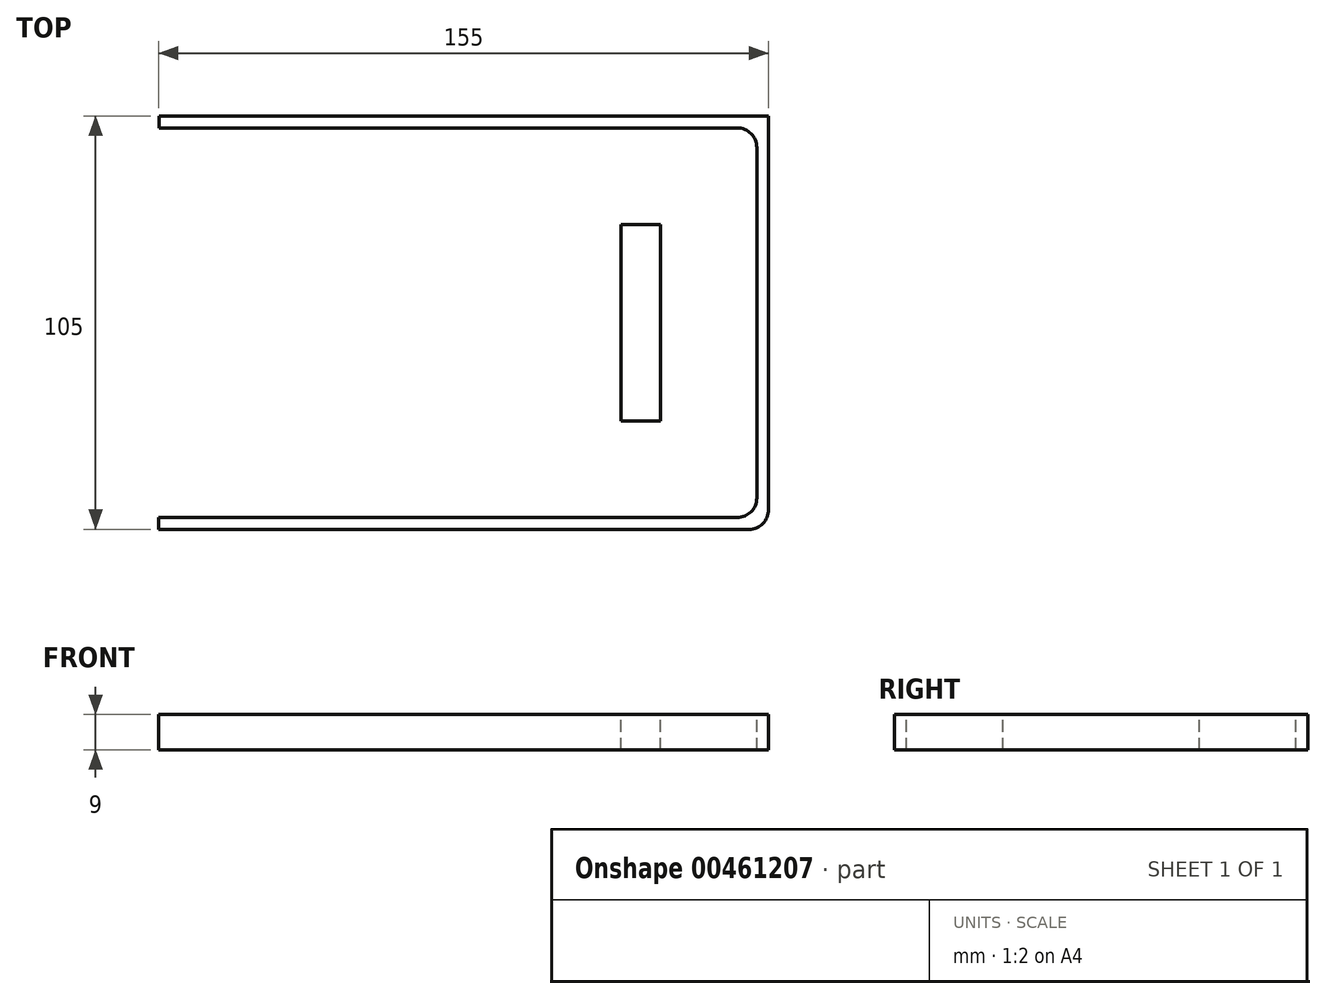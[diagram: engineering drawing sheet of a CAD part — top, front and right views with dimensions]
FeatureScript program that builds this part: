
annotation { "Feature Type Name" : "Feature", "Feature Type Description" : "" }
export const myFeature = defineFeature(function(context is Context, id is Id, definition is map)
    precondition{}
    {
        {
            var Q0;
            Q0=qCreatedBy(makeId("Top.planeOp"),FACE);
            var sketch = newSketch(context, id + "F0", { "sketchPlane" : qUnion([Q0])});
            skLineSegment(sketch, "E0.bottom", {"start": v(100, 75) * mm, "end": v(-100, 75) * mm});
            skLineSegment(sketch, "E0.top", {"start": v(100, -75) * mm, "end": v(-100, -75) * mm});
            skLineSegment(sketch, "E0.left", {"start": v(100, 75) * mm, "end": v(100, -75) * mm});
            skLineSegment(sketch, "E0.right", {"start": v(-100, 75) * mm, "end": v(-100, -75) * mm});
            skPoint(sketch, "E0.middle", {"position": v(0, 0) * mm});
            skSolve(sketch);
        }
        {
            var Q0;
            Q0=makeQuery(id+"F0.imprint","IMPRINT",FACE,{"disambiguationData":[TD([[makeQuery(id+"F0.imprint","IMPRINT",EDGE,{"derivedFrom":sQuery(id+"F0.wireOp",EDGE,"E0.bottom")}),1.0]])]});
            extrude(context, id + "F1", {"entities" : qUnion([Q0]), "depth" : 9 * mm, "offsetDistance" : 25 * mm});
        }
        {
            var Q0;
            Q0=makeQuery(id+"F1.opExtrude","CAP_FACE",FACE,{"disambiguationData":[OSD([sQuery(id+"F0.wireOp",EDGE,"E0.bottom"),sQuery(id+"F0.wireOp",EDGE,"E0.top"),sQuery(id+"F0.wireOp",EDGE,"E0.left"),sQuery(id+"F0.wireOp",EDGE,"E0.right")])],"isStart":false});
            var sketch = newSketch(context, id + "F2", { "sketchPlane" : qUnion([Q0])});
            skLineSegment(sketch, "E1.bottom", {"start": v(87.5, 60.44) * mm, "end": v(-87.5, 60.44) * mm});
            skLineSegment(sketch, "E1.top", {"start": v(87.5, -64.56) * mm, "end": v(-77.5, -64.56) * mm});
            skLineSegment(sketch, "E1.left", {"start": v(87.5, 60.44) * mm, "end": v(87.5, -64.56) * mm});
            skLineSegment(sketch, "E1.right", {"start": v(-87.5, 60.44) * mm, "end": v(-87.5, 34.72) * mm});
            skPoint(sketch, "E1.middle", {"position": v(0, -2.06) * mm});
            skLineSegment(sketch, "E2.bottom", {"start": v(-87.5, 29.72) * mm, "end": v(-46, 29.72) * mm});
            skLineSegment(sketch, "E3", {"start": v(-46, -38.28) * mm, "end": v(-87.5, -38.28) * mm});
            skLineSegment(sketch, "E4", {"start": v(-41, -38.28) * mm, "end": v(-46, -38.28) * mm});
            skLineSegment(sketch, "E5", {"start": v(-41, 34.72) * mm, "end": v(-87.5, 34.72) * mm});
            skLineSegment(sketch, "E6.trimOffspring", {"start": v(-87.5, -38.28) * mm, "end": v(-87.5, -64.56) * mm});
            skLineSegment(sketch, "E7", {"start": v(-6, -30.28) * mm, "end": v(-6, 26.72) * mm});
            skLineSegment(sketch, "E8", {"start": v(-74.36, 50.44) * mm, "end": v(60.64, 50.44) * mm});
            skLineSegment(sketch, "E9", {"start": v(60.64, 47.44) * mm, "end": v(-74.36, 47.44) * mm});
            skLineSegment(sketch, "E10", {"start": v(-74.36, 50.44) * mm, "end": v(-77.36, 50.44) * mm});
            skLineSegment(sketch, "E11", {"start": v(-77.36, 50.44) * mm, "end": v(-77.36, 47.44) * mm});
            skLineSegment(sketch, "E12", {"start": v(-77.36, 47.44) * mm, "end": v(-74.36, 47.44) * mm});
            skLineSegment(sketch, "E13", {"start": v(-87.5, -64.56) * mm, "end": v(-77.5, -64.56) * mm});
            skLineSegment(sketch, "E14", {"start": v(-77.5, -54.56) * mm, "end": v(60.64, -54.56) * mm});
            skLineSegment(sketch, "E15", {"start": v(60.64, -51.56) * mm, "end": v(-77.5, -51.56) * mm});
            skLineSegment(sketch, "E16", {"start": v(-77.5, -54.56) * mm, "end": v(-77.5, -51.56) * mm});
            skLineSegment(sketch, "E17", {"start": v(60.64, 47.44) * mm, "end": v(57.64, 47.44) * mm});
            skLineSegment(sketch, "E18", {"start": v(60.64, 50.44) * mm, "end": v(77.5, 50.44) * mm});
            skLineSegment(sketch, "E19", {"start": v(77.5, 50.44) * mm, "end": v(77.5, -54.56) * mm});
            skLineSegment(sketch, "E20", {"start": v(77.5, -54.56) * mm, "end": v(60.64, -54.56) * mm});
            skLineSegment(sketch, "E21", {"start": v(77.5, 50.44) * mm, "end": v(77.5, 47.44) * mm});
            skLineSegment(sketch, "E22", {"start": v(69.5, 47.44) * mm, "end": v(60.64, 47.44) * mm});
            skLineSegment(sketch, "E23", {"start": v(77.5, 50.44) * mm, "end": v(74.5, 50.44) * mm});
            skLineSegment(sketch, "E24", {"start": v(74.5, 42.44) * mm, "end": v(74.5, -46.56) * mm});
            skLineSegment(sketch, "E25", {"start": v(60.64, -51.56) * mm, "end": v(69.5, -51.56) * mm});
            skPoint(sketch, "E26.end.orphan", {"position": v(77.5, 48.67) * mm});
            skArc(sketch, "E27.filletArc", {"start": v(74.5, 42.44) * mm, "mid": v(73.03, 45.97) * mm, "end": v(69.5, 47.44) * mm});
            skPoint(sketch, "E28.visualSharp", {"position": v(74.5, -51.56) * mm});
            skArc(sketch, "E28.filletArc", {"start": v(69.5, -51.56) * mm, "mid": v(73.03, -50.1) * mm, "end": v(74.5, -46.56) * mm});
            skLineSegment(sketch, "E29", {"start": v(-87.5, 29.72) * mm, "end": v(-38.5, 29.72) * mm});
            skLineSegment(sketch, "E30", {"start": v(-38.5, 29.72) * mm, "end": v(-38.5, 26.72) * mm});
            skLineSegment(sketch, "E31", {"start": v(-38.5, 26.72) * mm, "end": v(-33.5, 26.72) * mm});
            skLineSegment(sketch, "E32", {"start": v(-33.5, 26.72) * mm, "end": v(-33.5, 34.72) * mm});
            skLineSegment(sketch, "E33", {"start": v(-33.5, 34.72) * mm, "end": v(-41, 34.72) * mm});
            skLineSegment(sketch, "E34", {"start": v(-100, -0.26) * mm, "end": v(-100, -3.86) * mm});
            skLineSegment(sketch, "E35", {"start": v(-100, -0.26) * mm, "end": v(-92.5, -0.26) * mm});
            skLineSegment(sketch, "E36", {"start": v(-100, -3.86) * mm, "end": v(-92.5, -3.86) * mm});
            skLineSegment(sketch, "E37", {"start": v(-87.5, -6.86) * mm, "end": v(-92.5, -3.86) * mm});
            skLineSegment(sketch, "E38", {"start": v(-92.5, -0.26) * mm, "end": v(-87.5, 2.74) * mm});
            skLineSegment(sketch, "E39", {"start": v(-87.5, 2.74) * mm, "end": v(-87.5, 29.72) * mm});
            skLineSegment(sketch, "E40", {"start": v(-87.5, -6.86) * mm, "end": v(-87.5, -33.28) * mm});
            skLineSegment(sketch, "E41", {"start": v(-87.5, -33.28) * mm, "end": v(-38.5, -33.28) * mm});
            skLineSegment(sketch, "E42", {"start": v(-38.5, -33.28) * mm, "end": v(-38.5, -30.28) * mm});
            skLineSegment(sketch, "E43", {"start": v(-38.5, -30.28) * mm, "end": v(-33.5, -30.28) * mm});
            skLineSegment(sketch, "E44", {"start": v(-33.5, -30.28) * mm, "end": v(-33.5, -38.28) * mm});
            skLineSegment(sketch, "E45", {"start": v(-33.5, -38.28) * mm, "end": v(-41, -38.28) * mm});
            skPoint(sketch, "E46.start.orphan", {"position": v(-41, -30.28) * mm});
            skLineSegment(sketch, "E47", {"start": v(0, -2.06) * mm, "end": v(40, -2.06) * mm});
            skLineSegment(sketch, "E48", {"start": v(40, -2.06) * mm, "end": v(40, 35.44) * mm});
            skLineSegment(sketch, "E49", {"start": v(40, -2.06) * mm, "end": v(40, -39.56) * mm});
            skPoint(sketch, "E50.end.orphan", {"position": v(42.97, -39.56) * mm});
            skLineSegment(sketch, "E51", {"start": v(40, 35.44) * mm, "end": v(50, 35.44) * mm});
            skLineSegment(sketch, "E52", {"start": v(50, 35.44) * mm, "end": v(50, -39.56) * mm});
            skLineSegment(sketch, "E53", {"start": v(50, -39.56) * mm, "end": v(40, -39.56) * mm});
            skLineSegment(sketch, "E54", {"start": v(40, -2.06) * mm, "end": v(40, 22.94) * mm});
            skLineSegment(sketch, "E55", {"start": v(40, 22.94) * mm, "end": v(50, 22.94) * mm});
            skLineSegment(sketch, "E56", {"start": v(40, -2.06) * mm, "end": v(40, -27.06) * mm});
            skLineSegment(sketch, "E57", {"start": v(40, -27.06) * mm, "end": v(50, -27.06) * mm});
            skSolve(sketch);
        }
        {
            var Q0;
            Q0=makeQuery(id+"F2.imprint","IMPRINT",FACE,{"disambiguationData":[TD([[makeQuery(id+"F2.imprint","IMPRINT",EDGE,{"derivedFrom":sQuery(id+"F2.wireOp",EDGE,"E1.bottom")}),1.0]])]});
            var Q1;
            Q1=makeQuery(id+"F2.imprint","IMPRINT",FACE,{"disambiguationData":[TD([[makeQuery(id+"F2.imprint","IMPRINT",EDGE,{"derivedFrom":sQuery(id+"F2.wireOp",EDGE,"E54")}),-1.0]])]});
            var Q2;
            Q2=makeQuery(id+"F2.imprint","IMPRINT",FACE,{"disambiguationData":[TD([[makeQuery(id+"F2.imprint","IMPRINT",EDGE,{"derivedFrom":sQuery(id+"F2.wireOp",EDGE,"E48")}),-1.0]])]});
            var Q3;
            Q3=makeQuery(id+"F2.imprint","IMPRINT",FACE,{"disambiguationData":[TD([[makeQuery(id+"F2.imprint","IMPRINT",EDGE,{"derivedFrom":sQuery(id+"F2.wireOp",EDGE,"E49")}),1.0]])]});
            var Q4;
            Q4=makeQuery(id+"F2.imprint","IMPRINT",FACE,{"disambiguationData":[TD([[makeQuery(id+"F2.imprint","IMPRINT",EDGE,{"derivedFrom":sQuery(id+"F2.wireOp",EDGE,"E1.bottom")}),-1.0]])]});
            extrude(context, id + "F3", {"entities" : qUnion([Q0, Q1, Q2, Q3, Q4]), "operationType" : NewBodyOperationType.REMOVE, "oppositeDirection" : true, "depth" : 25 * mm, "offsetDistance" : 25 * mm});
        }
        {
            var Q0;
            Q0=makeQuery(id+"F3.boolean.opBoolean","COPY",EDGE,{"derivedFrom":makeQuery(id+"F3.opExtrude","SWEPT_EDGE",EDGE,{"disambiguationData":[OSD([sQuery(id+"F2.wireOp",EDGE,"E21"),sQuery(id+"F2.wireOp",EDGE,"E23")])]})});
            var Q1;
            Q1=makeQuery(id+"F3.boolean.opBoolean","COPY",EDGE,{"derivedFrom":makeQuery(id+"F3.opExtrude","SWEPT_EDGE",EDGE,{"disambiguationData":[OSD([sQuery(id+"F2.wireOp",EDGE,"E19"),sQuery(id+"F2.wireOp",EDGE,"E20")])]})});
            fillet(context, id + "F4", {"entities" : qUnion([Q0, Q1]), "radius" : 5 * mm, "tangentPropagation" : true, "allowEdgeOverflow" : false});
        }
    });
